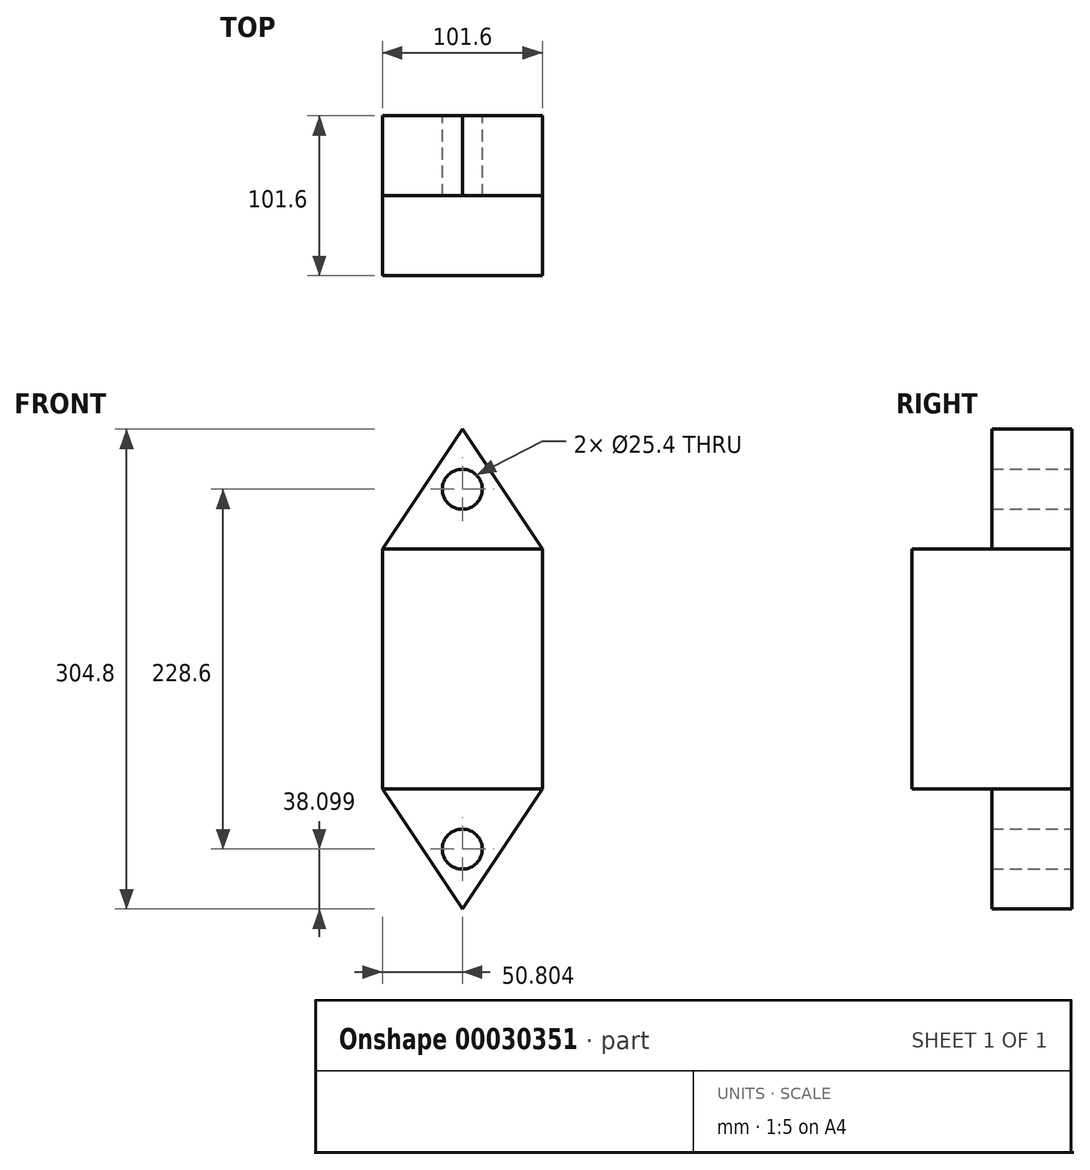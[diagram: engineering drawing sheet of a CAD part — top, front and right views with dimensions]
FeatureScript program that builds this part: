
annotation { "Feature Type Name" : "Feature", "Feature Type Description" : "" }
export const myFeature = defineFeature(function(context is Context, id is Id, definition is map)
    precondition{}
    {
        {
            var Q0;
            Q0=qCreatedBy(makeId("Front.planeOp"),FACE);
            var sketch = newSketch(context, id + "F0", { "sketchPlane" : qUnion([Q0])});
            skLineSegment(sketch, "E0.bottom", {"start": v(-20.5, 168.6) * mm, "end": v(81.1, 168.6) * mm});
            skLineSegment(sketch, "E0.top", {"start": v(-20.5, 16.2) * mm, "end": v(81.1, 16.2) * mm});
            skLineSegment(sketch, "E0.left", {"start": v(-20.5, 168.6) * mm, "end": v(-20.5, 16.2) * mm});
            skLineSegment(sketch, "E0.right", {"start": v(81.1, 168.6) * mm, "end": v(81.1, 16.2) * mm});
            skLineSegment(sketch, "E1", {"start": v(30.3, 168.6) * mm, "end": v(30.3, 244.8) * mm});
            skLineSegment(sketch, "E2", {"start": v(30.3, 244.8) * mm, "end": v(-20.5, 168.6) * mm});
            skLineSegment(sketch, "E3", {"start": v(30.3, 244.8) * mm, "end": v(81.1, 168.6) * mm});
            skCircle(sketch, "E4", {"center": v(30.3, 206.7) * mm, "radius": 12.7 * mm});
            skLineSegment(sketch, "E5", {"start": v(30.3, 16.2) * mm, "end": v(30.3, -60) * mm});
            skLineSegment(sketch, "E6", {"start": v(30.3, -60) * mm, "end": v(-20.5, 16.2) * mm});
            skLineSegment(sketch, "E7", {"start": v(30.3, -60) * mm, "end": v(81.1, 16.2) * mm});
            skCircle(sketch, "E8", {"center": v(30.3, -21.9) * mm, "radius": 12.7 * mm});
            skSolve(sketch);
        }
        {
            var Q0;
            Q0=makeQuery(id+"F0.imprint","IMPRINT",FACE,{"disambiguationData":[TD([[makeQuery(id+"F0.imprint","IMPRINT",EDGE,{"derivedFrom":sQuery(id+"F0.wireOp",EDGE,"E0.top")}),1.0]])]});
            extrude(context, id + "F1", {"entities" : qUnion([Q0]), "depth" : 101.6 * mm});
        }
        {
            var Q0;
            Q0=qSketchRegion(id+"F0",true);
            extrude(context, id + "F2", {"entities" : qUnion([Q0]), "operationType" : NewBodyOperationType.ADD, "depth" : 50.8 * mm});
        }
    });
